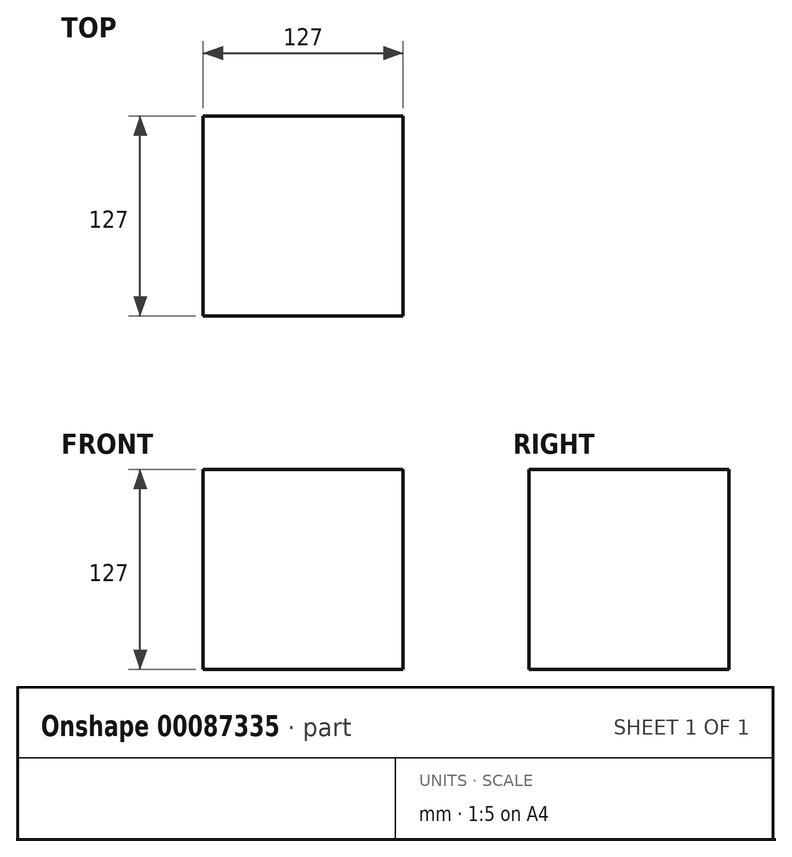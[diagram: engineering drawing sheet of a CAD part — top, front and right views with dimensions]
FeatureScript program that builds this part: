
annotation { "Feature Type Name" : "Feature", "Feature Type Description" : "" }
export const myFeature = defineFeature(function(context is Context, id is Id, definition is map)
    precondition{}
    {
        {
            var Q0;
            Q0=qCreatedBy(makeId("Front.planeOp"),FACE);
            var sketch = newSketch(context, id + "F0", { "sketchPlane" : qUnion([Q0])});
            skLineSegment(sketch, "E0.bottom", {"start": v(63.5, 63.5) * mm, "end": v(-63.5, 63.5) * mm});
            skLineSegment(sketch, "E0.top", {"start": v(63.5, -63.5) * mm, "end": v(-63.5, -63.5) * mm});
            skLineSegment(sketch, "E0.left", {"start": v(63.5, 63.5) * mm, "end": v(63.5, -63.5) * mm});
            skLineSegment(sketch, "E0.right", {"start": v(-63.5, 63.5) * mm, "end": v(-63.5, -63.5) * mm});
            skPoint(sketch, "E0.middle", {"position": v(0, 0) * mm});
            skSolve(sketch);
        }
        {
            var Q0;
            Q0=qSketchRegion(id+"F0",true);
            extrude(context, id + "F1", {"entities" : qUnion([Q0]), "depth" : 127 * mm});
        }
    });
